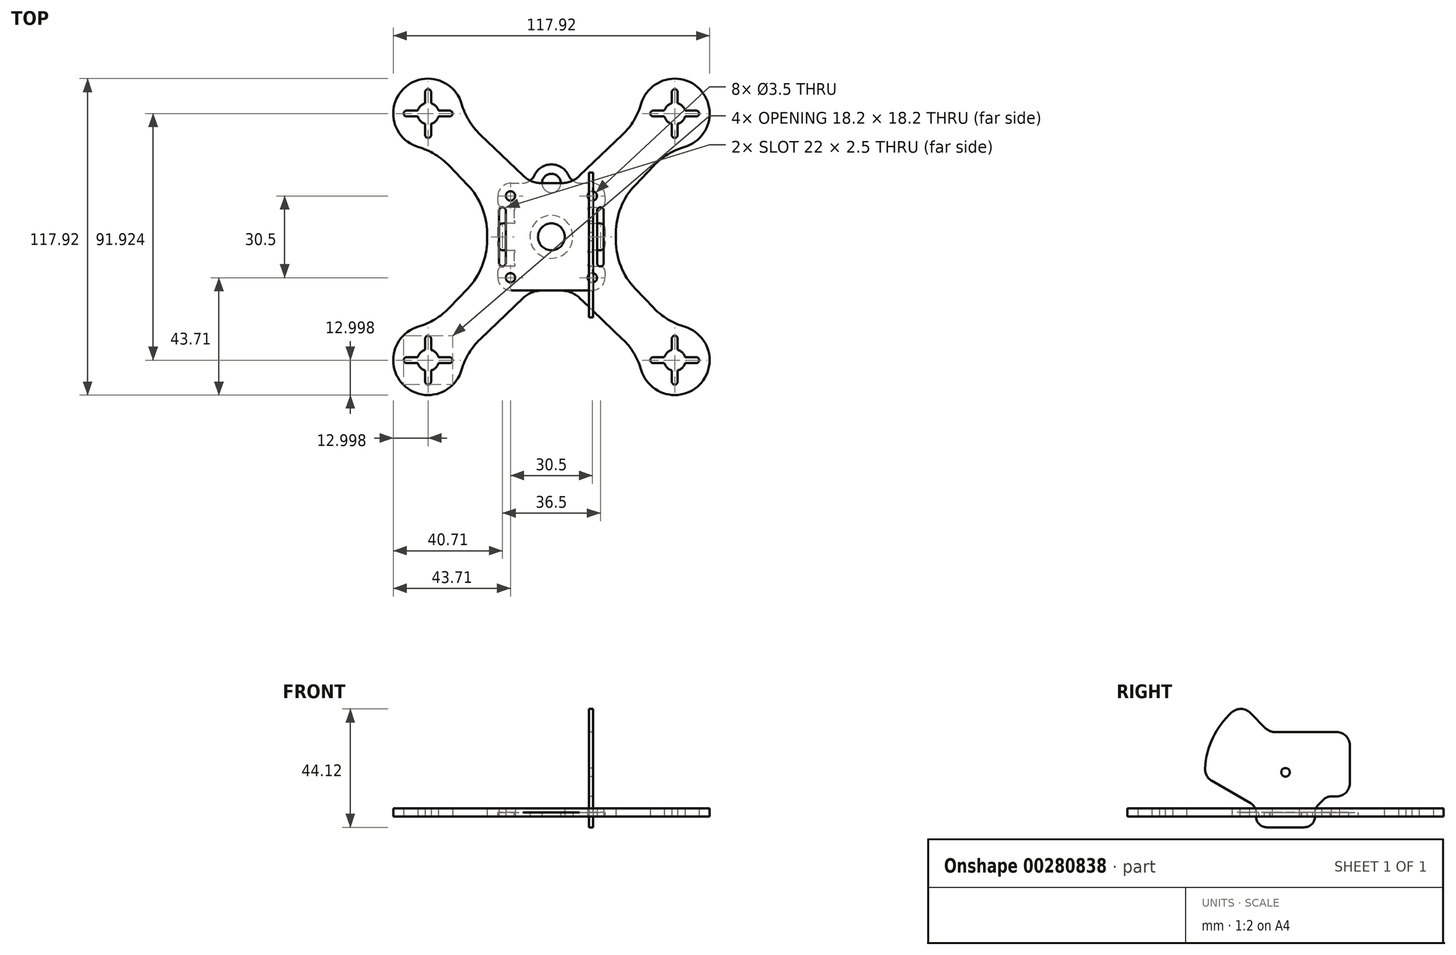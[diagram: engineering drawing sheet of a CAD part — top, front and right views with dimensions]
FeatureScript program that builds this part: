
annotation { "Feature Type Name" : "Feature", "Feature Type Description" : "" }
export const myFeature = defineFeature(function(context is Context, id is Id, definition is map)
    precondition{}
    {
        {
            var Q0;
            Q0=qCreatedBy(makeId("Top.planeOp"),FACE);
            var sketch = newSketch(context, id + "F0", { "sketchPlane" : qUnion([Q0])});
            skCircle(sketch, "E0", {"center": v(-45.96, 45.96) * mm, "radius": 38.1 * mm, "construction": true});
            skCircle(sketch, "E1", {"center": v(45.96, 45.96) * mm, "radius": 38.1 * mm, "construction": true});
            skCircle(sketch, "E2", {"center": v(-45.96, -45.96) * mm, "radius": 38.1 * mm, "construction": true});
            skCircle(sketch, "E3", {"center": v(45.96, -45.96) * mm, "radius": 38.1 * mm, "construction": true});
            skCircle(sketch, "E4", {"center": v(0, 0) * mm, "radius": 65 * mm, "construction": true});
            skLineSegment(sketch, "E5", {"start": v(0, 0) * mm, "end": v(-45.96, 45.96) * mm, "construction": true});
            skLineSegment(sketch, "E6", {"start": v(0, 0) * mm, "end": v(45.96, 45.96) * mm, "construction": true});
            skLineSegment(sketch, "E7", {"start": v(0, 0) * mm, "end": v(45.96, -45.96) * mm, "construction": true});
            skLineSegment(sketch, "E8", {"start": v(0, 0) * mm, "end": v(-45.96, -45.96) * mm, "construction": true});
            skCircle(sketch, "E9", {"center": v(-15.25, 15.25) * mm, "radius": 1.75 * mm});
            skCircle(sketch, "E10", {"center": v(15.25, 15.25) * mm, "radius": 1.75 * mm});
            skCircle(sketch, "E11", {"center": v(15.25, -15.25) * mm, "radius": 1.75 * mm});
            skCircle(sketch, "E12", {"center": v(-15.25, -15.25) * mm, "radius": 1.75 * mm});
            skArc(sketch, "E13", {"start": v(49.6, 33.48) * mm, "mid": v(55.15, 55.15) * mm, "end": v(33.48, 49.6) * mm});
            skLineSegment(sketch, "E14", {"start": v(26.5, 38.1) * mm, "end": v(10.5, 22.78) * mm});
            skLineSegment(sketch, "E15", {"start": v(38.1, 26.5) * mm, "end": v(31.22, 19.32) * mm});
            skPoint(sketch, "E16.visualSharp", {"position": v(33.06, 44.37) * mm});
            skArc(sketch, "E16.filletArc", {"start": v(26.5, 38.1) * mm, "mid": v(30.75, 43.39) * mm, "end": v(33.48, 49.6) * mm});
            skPoint(sketch, "E17.visualSharp", {"position": v(44.37, 33.06) * mm});
            skArc(sketch, "E17.filletArc", {"start": v(49.6, 33.48) * mm, "mid": v(43.39, 30.75) * mm, "end": v(38.1, 26.5) * mm});
            skArc(sketch, "E18", {"start": v(44.86, 49.8) * mm, "mid": v(43.13, 48.8) * mm, "end": v(42.12, 47.06) * mm});
            skLineSegment(sketch, "E19", {"start": v(45.96, 45.96) * mm, "end": v(32.12, 45.96) * mm, "construction": true});
            skLineSegment(sketch, "E20", {"start": v(45.96, 45.96) * mm, "end": v(45.96, 58.96) * mm, "construction": true});
            skLineSegment(sketch, "E21", {"start": v(45.96, 45.96) * mm, "end": v(58.96, 45.96) * mm, "construction": true});
            skLineSegment(sketch, "E22", {"start": v(45.96, 45.96) * mm, "end": v(45.96, 32.12) * mm, "construction": true});
            skArc(sketch, "E23", {"start": v(47.06, 53.96) * mm, "mid": v(45.96, 55.06) * mm, "end": v(44.86, 53.96) * mm});
            skLineSegment(sketch, "E24", {"start": v(44.86, 53.96) * mm, "end": v(44.86, 49.8) * mm});
            skLineSegment(sketch, "E25", {"start": v(47.06, 53.96) * mm, "end": v(47.06, 49.8) * mm});
            skArc(sketch, "E26", {"start": v(53.96, 44.86) * mm, "mid": v(55.06, 45.96) * mm, "end": v(53.96, 47.06) * mm});
            skArc(sketch, "E27", {"start": v(44.86, 37.96) * mm, "mid": v(45.96, 36.86) * mm, "end": v(47.06, 37.96) * mm});
            skArc(sketch, "E28", {"start": v(37.96, 47.06) * mm, "mid": v(36.86, 45.96) * mm, "end": v(37.96, 44.86) * mm});
            skLineSegment(sketch, "E29", {"start": v(44.86, 37.96) * mm, "end": v(44.86, 42.12) * mm});
            skLineSegment(sketch, "E30", {"start": v(37.96, 47.06) * mm, "end": v(42.12, 47.06) * mm});
            skLineSegment(sketch, "E31", {"start": v(37.96, 44.86) * mm, "end": v(42.12, 44.86) * mm});
            skLineSegment(sketch, "E32", {"start": v(53.96, 44.86) * mm, "end": v(49.8, 44.86) * mm});
            skLineSegment(sketch, "E33", {"start": v(47.06, 37.96) * mm, "end": v(47.06, 42.12) * mm});
            skLineSegment(sketch, "E34", {"start": v(53.96, 47.06) * mm, "end": v(49.8, 47.06) * mm});
            skArc(sketch, "E35.trimOffspring", {"start": v(42.12, 44.86) * mm, "mid": v(43.13, 43.13) * mm, "end": v(44.86, 42.12) * mm});
            skArc(sketch, "E36.trimOffspring", {"start": v(47.06, 42.12) * mm, "mid": v(48.8, 43.13) * mm, "end": v(49.8, 44.86) * mm});
            skArc(sketch, "E37.trimOffspring", {"start": v(49.8, 47.06) * mm, "mid": v(48.8, 48.8) * mm, "end": v(47.06, 49.8) * mm});
            skPoint(sketch, "E38.start.orphan", {"position": v(0, 12.73) * mm});
            skPoint(sketch, "E39.orphan", {"position": v(12.73, 0) * mm});
            skPoint(sketch, "E40.1.0", {"position": v(-33.06, 44.37) * mm});
            skPoint(sketch, "E40.1.1", {"position": v(-44.37, 33.06) * mm});
            skArc(sketch, "E40.1.2", {"start": v(-33.48, 49.6) * mm, "mid": v(-55.15, 55.15) * mm, "end": v(-49.6, 33.48) * mm});
            skArc(sketch, "E40.1.3", {"start": v(-33.48, 49.6) * mm, "mid": v(-30.75, 43.39) * mm, "end": v(-26.5, 38.1) * mm});
            skLineSegment(sketch, "E40.1.4", {"start": v(-45.96, 45.96) * mm, "end": v(-45.96, 58.96) * mm, "construction": true});
            skLineSegment(sketch, "E40.1.5", {"start": v(-45.96, 45.96) * mm, "end": v(-32.12, 45.96) * mm, "construction": true});
            skLineSegment(sketch, "E40.1.6", {"start": v(-45.96, 45.96) * mm, "end": v(-45.96, 32.12) * mm, "construction": true});
            skLineSegment(sketch, "E40.1.7", {"start": v(-45.96, 45.96) * mm, "end": v(-58.96, 45.96) * mm, "construction": true});
            skLineSegment(sketch, "E40.1.8", {"start": v(-44.86, 37.96) * mm, "end": v(-44.86, 42.12) * mm});
            skLineSegment(sketch, "E40.1.9", {"start": v(-53.96, 44.86) * mm, "end": v(-49.8, 44.86) * mm});
            skLineSegment(sketch, "E40.1.10", {"start": v(-47.06, 37.96) * mm, "end": v(-47.06, 42.12) * mm});
            skArc(sketch, "E40.1.11", {"start": v(-42.12, 47.06) * mm, "mid": v(-43.13, 48.8) * mm, "end": v(-44.86, 49.8) * mm});
            skLineSegment(sketch, "E40.1.12", {"start": v(-37.96, 47.06) * mm, "end": v(-42.12, 47.06) * mm});
            skArc(sketch, "E40.1.13", {"start": v(-47.06, 37.96) * mm, "mid": v(-45.96, 36.86) * mm, "end": v(-44.86, 37.96) * mm});
            skArc(sketch, "E40.1.14", {"start": v(-37.96, 44.86) * mm, "mid": v(-36.86, 45.96) * mm, "end": v(-37.96, 47.06) * mm});
            skLineSegment(sketch, "E40.1.15", {"start": v(-44.86, 53.96) * mm, "end": v(-44.86, 49.8) * mm});
            skLineSegment(sketch, "E40.1.16", {"start": v(-47.06, 53.96) * mm, "end": v(-47.06, 49.8) * mm});
            skArc(sketch, "E40.1.17", {"start": v(-47.06, 49.8) * mm, "mid": v(-48.8, 48.8) * mm, "end": v(-49.8, 47.06) * mm});
            skLineSegment(sketch, "E40.1.18", {"start": v(-53.96, 47.06) * mm, "end": v(-49.8, 47.06) * mm});
            skArc(sketch, "E40.1.19", {"start": v(-53.96, 47.06) * mm, "mid": v(-55.06, 45.96) * mm, "end": v(-53.96, 44.86) * mm});
            skArc(sketch, "E40.1.20", {"start": v(-44.86, 42.12) * mm, "mid": v(-43.13, 43.13) * mm, "end": v(-42.12, 44.86) * mm});
            skLineSegment(sketch, "E40.1.21", {"start": v(-37.96, 44.86) * mm, "end": v(-42.12, 44.86) * mm});
            skArc(sketch, "E40.1.22", {"start": v(-49.8, 44.86) * mm, "mid": v(-48.8, 43.13) * mm, "end": v(-47.06, 42.12) * mm});
            skArc(sketch, "E40.1.23", {"start": v(-44.86, 53.96) * mm, "mid": v(-45.96, 55.06) * mm, "end": v(-47.06, 53.96) * mm});
            skArc(sketch, "E40.1.24", {"start": v(-38.1, 26.5) * mm, "mid": v(-43.39, 30.75) * mm, "end": v(-49.6, 33.48) * mm});
            skLineSegment(sketch, "E40.1.25", {"start": v(-38.1, 26.5) * mm, "end": v(-31.22, 19.32) * mm});
            skLineSegment(sketch, "E40.1.26", {"start": v(-26.5, 38.1) * mm, "end": v(-10.5, 22.78) * mm});
            skPoint(sketch, "E40.2.0", {"position": v(-44.37, -33.06) * mm});
            skPoint(sketch, "E40.2.1", {"position": v(-33.06, -44.37) * mm});
            skArc(sketch, "E40.2.2", {"start": v(-49.6, -33.48) * mm, "mid": v(-55.15, -55.15) * mm, "end": v(-33.48, -49.6) * mm});
            skArc(sketch, "E40.2.3", {"start": v(-49.6, -33.48) * mm, "mid": v(-43.39, -30.75) * mm, "end": v(-38.1, -26.5) * mm});
            skLineSegment(sketch, "E40.2.4", {"start": v(-45.96, -45.96) * mm, "end": v(-58.96, -45.96) * mm, "construction": true});
            skLineSegment(sketch, "E40.2.5", {"start": v(-45.96, -45.96) * mm, "end": v(-45.96, -32.12) * mm, "construction": true});
            skLineSegment(sketch, "E40.2.6", {"start": v(-45.96, -45.96) * mm, "end": v(-32.12, -45.96) * mm, "construction": true});
            skLineSegment(sketch, "E40.2.7", {"start": v(-45.96, -45.96) * mm, "end": v(-45.96, -58.96) * mm, "construction": true});
            skLineSegment(sketch, "E40.2.8", {"start": v(-37.96, -44.86) * mm, "end": v(-42.12, -44.86) * mm});
            skLineSegment(sketch, "E40.2.9", {"start": v(-44.86, -53.96) * mm, "end": v(-44.86, -49.8) * mm});
            skLineSegment(sketch, "E40.2.10", {"start": v(-37.96, -47.06) * mm, "end": v(-42.12, -47.06) * mm});
            skArc(sketch, "E40.2.11", {"start": v(-47.06, -42.12) * mm, "mid": v(-48.8, -43.13) * mm, "end": v(-49.8, -44.86) * mm});
            skLineSegment(sketch, "E40.2.12", {"start": v(-47.06, -37.96) * mm, "end": v(-47.06, -42.12) * mm});
            skArc(sketch, "E40.2.13", {"start": v(-37.96, -47.06) * mm, "mid": v(-36.86, -45.96) * mm, "end": v(-37.96, -44.86) * mm});
            skArc(sketch, "E40.2.14", {"start": v(-44.86, -37.96) * mm, "mid": v(-45.96, -36.86) * mm, "end": v(-47.06, -37.96) * mm});
            skLineSegment(sketch, "E40.2.15", {"start": v(-53.96, -44.86) * mm, "end": v(-49.8, -44.86) * mm});
            skLineSegment(sketch, "E40.2.16", {"start": v(-53.96, -47.06) * mm, "end": v(-49.8, -47.06) * mm});
            skArc(sketch, "E40.2.17", {"start": v(-49.8, -47.06) * mm, "mid": v(-48.8, -48.8) * mm, "end": v(-47.06, -49.8) * mm});
            skLineSegment(sketch, "E40.2.18", {"start": v(-47.06, -53.96) * mm, "end": v(-47.06, -49.8) * mm});
            skArc(sketch, "E40.2.19", {"start": v(-47.06, -53.96) * mm, "mid": v(-45.96, -55.06) * mm, "end": v(-44.86, -53.96) * mm});
            skArc(sketch, "E40.2.20", {"start": v(-42.12, -44.86) * mm, "mid": v(-43.13, -43.13) * mm, "end": v(-44.86, -42.12) * mm});
            skLineSegment(sketch, "E40.2.21", {"start": v(-44.86, -37.96) * mm, "end": v(-44.86, -42.12) * mm});
            skArc(sketch, "E40.2.22", {"start": v(-44.86, -49.8) * mm, "mid": v(-43.13, -48.8) * mm, "end": v(-42.12, -47.06) * mm});
            skArc(sketch, "E40.2.23", {"start": v(-53.96, -44.86) * mm, "mid": v(-55.06, -45.96) * mm, "end": v(-53.96, -47.06) * mm});
            skArc(sketch, "E40.2.24", {"start": v(-26.5, -38.1) * mm, "mid": v(-30.75, -43.39) * mm, "end": v(-33.48, -49.6) * mm});
            skLineSegment(sketch, "E40.2.25", {"start": v(-26.5, -38.1) * mm, "end": v(-10.5, -22.78) * mm});
            skLineSegment(sketch, "E40.2.26", {"start": v(-38.1, -26.5) * mm, "end": v(-31.22, -19.32) * mm});
            skPoint(sketch, "E40.3.0", {"position": v(33.06, -44.37) * mm});
            skPoint(sketch, "E40.3.1", {"position": v(44.37, -33.06) * mm});
            skArc(sketch, "E40.3.2", {"start": v(33.48, -49.6) * mm, "mid": v(55.15, -55.15) * mm, "end": v(49.6, -33.48) * mm});
            skArc(sketch, "E40.3.3", {"start": v(33.48, -49.6) * mm, "mid": v(30.75, -43.39) * mm, "end": v(26.5, -38.1) * mm});
            skLineSegment(sketch, "E40.3.4", {"start": v(45.96, -45.96) * mm, "end": v(45.96, -58.96) * mm, "construction": true});
            skLineSegment(sketch, "E40.3.5", {"start": v(45.96, -45.96) * mm, "end": v(32.12, -45.96) * mm, "construction": true});
            skLineSegment(sketch, "E40.3.6", {"start": v(45.96, -45.96) * mm, "end": v(45.96, -32.12) * mm, "construction": true});
            skLineSegment(sketch, "E40.3.7", {"start": v(45.96, -45.96) * mm, "end": v(58.96, -45.96) * mm, "construction": true});
            skLineSegment(sketch, "E40.3.8", {"start": v(44.86, -37.96) * mm, "end": v(44.86, -42.12) * mm});
            skLineSegment(sketch, "E40.3.9", {"start": v(53.96, -44.86) * mm, "end": v(49.8, -44.86) * mm});
            skLineSegment(sketch, "E40.3.10", {"start": v(47.06, -37.96) * mm, "end": v(47.06, -42.12) * mm});
            skArc(sketch, "E40.3.11", {"start": v(42.12, -47.06) * mm, "mid": v(43.13, -48.8) * mm, "end": v(44.86, -49.8) * mm});
            skLineSegment(sketch, "E40.3.12", {"start": v(37.96, -47.06) * mm, "end": v(42.12, -47.06) * mm});
            skArc(sketch, "E40.3.13", {"start": v(47.06, -37.96) * mm, "mid": v(45.96, -36.86) * mm, "end": v(44.86, -37.96) * mm});
            skArc(sketch, "E40.3.14", {"start": v(37.96, -44.86) * mm, "mid": v(36.86, -45.96) * mm, "end": v(37.96, -47.06) * mm});
            skLineSegment(sketch, "E40.3.15", {"start": v(44.86, -53.96) * mm, "end": v(44.86, -49.8) * mm});
            skLineSegment(sketch, "E40.3.16", {"start": v(47.06, -53.96) * mm, "end": v(47.06, -49.8) * mm});
            skArc(sketch, "E40.3.17", {"start": v(47.06, -49.8) * mm, "mid": v(48.8, -48.8) * mm, "end": v(49.8, -47.06) * mm});
            skLineSegment(sketch, "E40.3.18", {"start": v(53.96, -47.06) * mm, "end": v(49.8, -47.06) * mm});
            skArc(sketch, "E40.3.19", {"start": v(53.96, -47.06) * mm, "mid": v(55.06, -45.96) * mm, "end": v(53.96, -44.86) * mm});
            skArc(sketch, "E40.3.20", {"start": v(44.86, -42.12) * mm, "mid": v(43.13, -43.13) * mm, "end": v(42.12, -44.86) * mm});
            skLineSegment(sketch, "E40.3.21", {"start": v(37.96, -44.86) * mm, "end": v(42.12, -44.86) * mm});
            skArc(sketch, "E40.3.22", {"start": v(49.8, -44.86) * mm, "mid": v(48.8, -43.13) * mm, "end": v(47.06, -42.12) * mm});
            skArc(sketch, "E40.3.23", {"start": v(44.86, -53.96) * mm, "mid": v(45.96, -55.06) * mm, "end": v(47.06, -53.96) * mm});
            skArc(sketch, "E40.3.24", {"start": v(38.1, -26.5) * mm, "mid": v(43.39, -30.75) * mm, "end": v(49.6, -33.48) * mm});
            skLineSegment(sketch, "E40.3.25", {"start": v(38.1, -26.5) * mm, "end": v(31.22, -19.32) * mm});
            skLineSegment(sketch, "E40.3.26", {"start": v(26.5, -38.1) * mm, "end": v(10.5, -22.78) * mm});
            skLineSegment(sketch, "E41.trimOffspring", {"start": v(-3.58, 20) * mm, "end": v(3.58, 20) * mm});
            skLineSegment(sketch, "E42.trimOffspring", {"start": v(-3.58, -20) * mm, "end": v(3.58, -20) * mm});
            skLineSegment(sketch, "E43.bottom", {"start": v(-19.5, 11) * mm, "end": v(-17, 11) * mm});
            skLineSegment(sketch, "E43.top", {"start": v(-19.5, -11) * mm, "end": v(-17, -11) * mm});
            skLineSegment(sketch, "E43.right", {"start": v(-17, 11) * mm, "end": v(-17, -11) * mm});
            skLineSegment(sketch, "E44.bottom", {"start": v(19.5, 11) * mm, "end": v(17, 11) * mm});
            skLineSegment(sketch, "E44.top", {"start": v(19.5, -11) * mm, "end": v(17, -11) * mm});
            skLineSegment(sketch, "E44.right", {"start": v(17, 11) * mm, "end": v(17, -11) * mm});
            skLineSegment(sketch, "E45", {"start": v(-19.5, 11) * mm, "end": v(-19.5, -11) * mm});
            skLineSegment(sketch, "E46", {"start": v(19.5, 11) * mm, "end": v(19.5, -11) * mm});
            skLineSegment(sketch, "E47", {"start": v(-24, 1.34) * mm, "end": v(-24, -1.34) * mm});
            skLineSegment(sketch, "E48", {"start": v(24, 1.34) * mm, "end": v(24, -1.34) * mm});
            skPoint(sketch, "E49.visualSharp", {"position": v(-24, 11.78) * mm});
            skArc(sketch, "E49.filletArc", {"start": v(-24, 1.34) * mm, "mid": v(-25.87, 11.02) * mm, "end": v(-31.22, 19.32) * mm});
            skPoint(sketch, "E50.visualSharp", {"position": v(-24, -11.78) * mm});
            skArc(sketch, "E50.filletArc", {"start": v(-31.22, -19.32) * mm, "mid": v(-25.87, -11.02) * mm, "end": v(-24, -1.34) * mm});
            skPoint(sketch, "E51.visualSharp", {"position": v(24, -11.78) * mm});
            skArc(sketch, "E51.filletArc", {"start": v(24, -1.34) * mm, "mid": v(25.87, -11.02) * mm, "end": v(31.22, -19.32) * mm});
            skPoint(sketch, "E52.visualSharp", {"position": v(24, 11.78) * mm});
            skArc(sketch, "E52.filletArc", {"start": v(31.22, 19.32) * mm, "mid": v(25.87, 11.02) * mm, "end": v(24, 1.34) * mm});
            skPoint(sketch, "E53.visualSharp", {"position": v(-7.6, 20) * mm});
            skArc(sketch, "E53.filletArc", {"start": v(-10.5, 22.78) * mm, "mid": v(-7.3, 20.72) * mm, "end": v(-3.58, 20) * mm});
            skPoint(sketch, "E54.visualSharp", {"position": v(7.6, 20) * mm});
            skArc(sketch, "E54.filletArc", {"start": v(3.58, 20) * mm, "mid": v(7.3, 20.72) * mm, "end": v(10.5, 22.78) * mm});
            skPoint(sketch, "E55.visualSharp", {"position": v(-7.6, -20) * mm});
            skArc(sketch, "E55.filletArc", {"start": v(-3.58, -20) * mm, "mid": v(-7.3, -20.72) * mm, "end": v(-10.5, -22.78) * mm});
            skPoint(sketch, "E56.visualSharp", {"position": v(7.6, -20) * mm});
            skArc(sketch, "E56.filletArc", {"start": v(10.5, -22.78) * mm, "mid": v(7.3, -20.72) * mm, "end": v(3.58, -20) * mm});
            skCircle(sketch, "E57", {"center": v(0, 0) * mm, "radius": 5 * mm});
            skSolve(sketch);
        }
        {
            var Q0;
            Q0 = qSketchRegion(id + "F0", true);
            extrude(context, id + "F1", {"entities" : qUnion([Q0]), "depth" : 3 * mm});
        }
        {
            var Q0;
            Q0=qCreatedBy(makeId("Top.planeOp"),FACE);
            var sketch = newSketch(context, id + "F2", { "sketchPlane" : qUnion([Q0])});
            skLineSegment(sketch, "E58.bottom", {"start": v(-15, 20) * mm, "end": v(-10.9, 20) * mm});
            skLineSegment(sketch, "E58.top", {"start": v(-15, -20) * mm, "end": v(15, -20) * mm});
            skLineSegment(sketch, "E58.left", {"start": v(-20, 15) * mm, "end": v(-20, 13) * mm});
            skLineSegment(sketch, "E58.right", {"start": v(20, 15) * mm, "end": v(20, 13) * mm});
            skLineSegment(sketch, "E59", {"start": v(-20, 20) * mm, "end": v(20, -20) * mm, "construction": true});
            skLineSegment(sketch, "E60", {"start": v(-20, -20) * mm, "end": v(20, 20) * mm, "construction": true});
            skPoint(sketch, "E61.visualSharp", {"position": v(-20, 20) * mm});
            skArc(sketch, "E61.filletArc", {"start": v(-15, 20) * mm, "mid": v(-18.54, 18.54) * mm, "end": v(-20, 15) * mm});
            skPoint(sketch, "E62.visualSharp", {"position": v(20, 20) * mm});
            skArc(sketch, "E62.filletArc", {"start": v(20, 15) * mm, "mid": v(18.54, 18.54) * mm, "end": v(15, 20) * mm});
            skPoint(sketch, "E63.visualSharp", {"position": v(20, -20) * mm});
            skArc(sketch, "E63.filletArc", {"start": v(15, -20) * mm, "mid": v(18.54, -18.54) * mm, "end": v(20, -15) * mm});
            skPoint(sketch, "E64.visualSharp", {"position": v(-20, -20) * mm});
            skArc(sketch, "E64.filletArc", {"start": v(-20, -15) * mm, "mid": v(-18.54, -18.54) * mm, "end": v(-15, -20) * mm});
            skCircle(sketch, "E65", {"center": v(-15.25, -15.25) * mm, "radius": 1.75 * mm});
            skCircle(sketch, "E66", {"center": v(15.25, -15.25) * mm, "radius": 1.75 * mm});
            skCircle(sketch, "E67", {"center": v(15.25, 15.25) * mm, "radius": 1.75 * mm});
            skCircle(sketch, "E68", {"center": v(-15.25, 15.25) * mm, "radius": 1.75 * mm});
            skLineSegment(sketch, "E69", {"start": v(14, 10) * mm, "end": v(14, 6) * mm});
            skLineSegment(sketch, "E70", {"start": v(-14, 10) * mm, "end": v(-14, 6) * mm});
            skLineSegment(sketch, "E71", {"start": v(14, 11) * mm, "end": v(18, 11) * mm});
            skLineSegment(sketch, "E72", {"start": v(14, -11) * mm, "end": v(18, -11) * mm});
            skLineSegment(sketch, "E73", {"start": v(-14, 11) * mm, "end": v(-18, 11) * mm});
            skLineSegment(sketch, "E74", {"start": v(-14, -11) * mm, "end": v(-18, -11) * mm});
            skLineSegment(sketch, "E75.trimOffspring", {"start": v(-20, -13) * mm, "end": v(-20, -15) * mm});
            skLineSegment(sketch, "E76.trimOffspring", {"start": v(20, -13) * mm, "end": v(20, -15) * mm});
            skLineSegment(sketch, "E77", {"start": v(-14, 5) * mm, "end": v(-18, 5) * mm});
            skLineSegment(sketch, "E78", {"start": v(-20, 3) * mm, "end": v(-20, -3) * mm});
            skLineSegment(sketch, "E79", {"start": v(-18, -5) * mm, "end": v(-14, -5) * mm});
            skLineSegment(sketch, "E80", {"start": v(14, 5) * mm, "end": v(18, 5) * mm});
            skLineSegment(sketch, "E81", {"start": v(20, 3) * mm, "end": v(20, -3) * mm});
            skLineSegment(sketch, "E82", {"start": v(18, -5) * mm, "end": v(14, -5) * mm});
            skLineSegment(sketch, "E83.trimOffspring", {"start": v(-14, -6) * mm, "end": v(-14, -10) * mm});
            skLineSegment(sketch, "E84.trimOffspring", {"start": v(14, -6) * mm, "end": v(14, -10) * mm});
            skArc(sketch, "E85", {"start": v(-14, 5) * mm, "mid": v(-13.5, 5.5) * mm, "end": v(-14, 6) * mm});
            skArc(sketch, "E86", {"start": v(-14, 10) * mm, "mid": v(-13.5, 10.5) * mm, "end": v(-14, 11) * mm});
            skArc(sketch, "E87", {"start": v(-14, -6) * mm, "mid": v(-13.5, -5.5) * mm, "end": v(-14, -5) * mm});
            skArc(sketch, "E88", {"start": v(-14, -11) * mm, "mid": v(-13.5, -10.5) * mm, "end": v(-14, -10) * mm});
            skArc(sketch, "E89", {"start": v(14, -5) * mm, "mid": v(13.5, -5.5) * mm, "end": v(14, -6) * mm});
            skArc(sketch, "E90", {"start": v(14, -10) * mm, "mid": v(13.5, -10.5) * mm, "end": v(14, -11) * mm});
            skArc(sketch, "E91", {"start": v(14, 11) * mm, "mid": v(13.5, 10.5) * mm, "end": v(14, 10) * mm});
            skArc(sketch, "E92", {"start": v(14, 6) * mm, "mid": v(13.5, 5.5) * mm, "end": v(14, 5) * mm});
            skPoint(sketch, "E93.visualSharp", {"position": v(-20, 5) * mm});
            skArc(sketch, "E93.filletArc", {"start": v(-18, 5) * mm, "mid": v(-19.41, 4.41) * mm, "end": v(-20, 3) * mm});
            skPoint(sketch, "E94.visualSharp", {"position": v(-20, -5) * mm});
            skArc(sketch, "E94.filletArc", {"start": v(-20, -3) * mm, "mid": v(-19.41, -4.41) * mm, "end": v(-18, -5) * mm});
            skPoint(sketch, "E95.visualSharp", {"position": v(-20, -11) * mm});
            skArc(sketch, "E95.filletArc", {"start": v(-18, -11) * mm, "mid": v(-19.41, -11.59) * mm, "end": v(-20, -13) * mm});
            skPoint(sketch, "E96.visualSharp", {"position": v(-20, 11) * mm});
            skArc(sketch, "E96.filletArc", {"start": v(-20, 13) * mm, "mid": v(-19.41, 11.59) * mm, "end": v(-18, 11) * mm});
            skPoint(sketch, "E97.visualSharp", {"position": v(20, 11) * mm});
            skArc(sketch, "E97.filletArc", {"start": v(18, 11) * mm, "mid": v(19.41, 11.59) * mm, "end": v(20, 13) * mm});
            skPoint(sketch, "E98.visualSharp", {"position": v(20, 5) * mm});
            skArc(sketch, "E98.filletArc", {"start": v(20, 3) * mm, "mid": v(19.41, 4.41) * mm, "end": v(18, 5) * mm});
            skPoint(sketch, "E99.visualSharp", {"position": v(20, -5) * mm});
            skArc(sketch, "E99.filletArc", {"start": v(18, -5) * mm, "mid": v(19.41, -4.41) * mm, "end": v(20, -3) * mm});
            skPoint(sketch, "E100.visualSharp", {"position": v(20, -11) * mm});
            skArc(sketch, "E100.filletArc", {"start": v(20, -13) * mm, "mid": v(19.41, -11.59) * mm, "end": v(18, -11) * mm});
            skCircle(sketch, "E101", {"center": v(0, 0) * mm, "radius": 8 * mm});
            skCircle(sketch, "E102", {"center": v(0, 20) * mm, "radius": 3.5 * mm});
            skArc(sketch, "E103", {"start": v(6.36, 22.92) * mm, "mid": v(0, 27) * mm, "end": v(-6.36, 22.92) * mm});
            skLineSegment(sketch, "E104.trimOffspring", {"start": v(10.9, 20) * mm, "end": v(15, 20) * mm});
            skPoint(sketch, "E105.visualSharp", {"position": v(-7, 20) * mm});
            skArc(sketch, "E105.filletArc", {"start": v(-10.9, 20) * mm, "mid": v(-8.2, 20.8) * mm, "end": v(-6.36, 22.92) * mm});
            skPoint(sketch, "E106.visualSharp", {"position": v(7, 20) * mm});
            skArc(sketch, "E106.filletArc", {"start": v(6.36, 22.92) * mm, "mid": v(8.2, 20.8) * mm, "end": v(10.9, 20) * mm});
            skSolve(sketch);
        }
        {
            var Q0;
            Q0 = qSketchRegion(id + "F2", true);
            extrude(context, id + "F3", {"entities" : qUnion([Q0]), "depth" : 1.5 * mm});
        }
        {
            var Q0;
            Q0=makeQuery(id+"F1.opExtrude","SWEPT_EDGE",EDGE,{"disambiguationData":[OSD([sQuery(id+"F0.wireOp",EDGE,"E43.bottom"),sQuery(id+"F0.wireOp",EDGE,"E45")])]});
            var Q1;
            Q1=makeQuery(id+"F1.opExtrude","SWEPT_EDGE",EDGE,{"disambiguationData":[OSD([sQuery(id+"F0.wireOp",EDGE,"E43.bottom"),sQuery(id+"F0.wireOp",EDGE,"E43.right")])]});
            var Q2;
            Q2=makeQuery(id+"F1.opExtrude","SWEPT_EDGE",EDGE,{"disambiguationData":[OSD([sQuery(id+"F0.wireOp",EDGE,"E43.top"),sQuery(id+"F0.wireOp",EDGE,"E45")])]});
            var Q3;
            Q3=makeQuery(id+"F1.opExtrude","SWEPT_EDGE",EDGE,{"disambiguationData":[OSD([sQuery(id+"F0.wireOp",EDGE,"E43.top"),sQuery(id+"F0.wireOp",EDGE,"E43.right")])]});
            var Q4;
            Q4=makeQuery(id+"F1.opExtrude","SWEPT_EDGE",EDGE,{"disambiguationData":[OSD([sQuery(id+"F0.wireOp",EDGE,"E44.top"),sQuery(id+"F0.wireOp",EDGE,"E44.right")])]});
            var Q5;
            Q5=makeQuery(id+"F1.opExtrude","SWEPT_EDGE",EDGE,{"disambiguationData":[OSD([sQuery(id+"F0.wireOp",EDGE,"E44.top"),sQuery(id+"F0.wireOp",EDGE,"E46")])]});
            var Q6;
            Q6=makeQuery(id+"F1.opExtrude","SWEPT_EDGE",EDGE,{"disambiguationData":[OSD([sQuery(id+"F0.wireOp",EDGE,"E44.bottom"),sQuery(id+"F0.wireOp",EDGE,"E44.right")])]});
            var Q7;
            Q7=makeQuery(id+"F1.opExtrude","SWEPT_EDGE",EDGE,{"disambiguationData":[OSD([sQuery(id+"F0.wireOp",EDGE,"E44.bottom"),sQuery(id+"F0.wireOp",EDGE,"E46")])]});
            fillet(context, id + "F4", {"entities" : qUnion([Q0, Q1, Q2, Q3, Q4, Q5, Q6, Q7]), "radius" : 1.25 * mm, "tangentPropagation" : true, "allowEdgeOverflow" : false});
        }
        {
            var Q0;
            Q0=qCreatedBy(makeId("Right.planeOp"),FACE);
            cPlane(context, id + "F5", {"entities" : qUnion([Q0]), "cplaneType" : CPlaneType.OFFSET, "offset" : 14 * mm, "width" : 150 * mm, "height" : 150 * mm});
        }
        {
            var Q0;
            Q0=qCreatedBy(id+"F5.planeOp",FACE);
            var sketch = newSketch(context, id + "F6", { "sketchPlane" : qUnion([Q0])});
            skLineSegment(sketch, "E107.bottom", {"start": v(-5.75, 1.5) * mm, "end": v(5.75, 1.5) * mm});
            skLineSegment(sketch, "E107.top", {"start": v(-5.75, 0) * mm, "end": v(5.75, 0) * mm});
            skLineSegment(sketch, "E107.left", {"start": v(-5.75, 1.5) * mm, "end": v(-5.75, 0) * mm});
            skLineSegment(sketch, "E107.right", {"start": v(5.75, 1.5) * mm, "end": v(5.75, 0) * mm});
            skLineSegment(sketch, "E108.top", {"start": v(-7, -4) * mm, "end": v(7, -4) * mm});
            skLineSegment(sketch, "E108.left", {"start": v(-11, 1.5) * mm, "end": v(-11, 0) * mm});
            skLineSegment(sketch, "E108.right", {"start": v(11, 1.5) * mm, "end": v(11, 0) * mm});
            skArc(sketch, "E109", {"start": v(-11, 1.5) * mm, "mid": v(-11.54, 3.5) * mm, "end": v(-13, 4.96) * mm});
            skArc(sketch, "E110", {"start": v(12.17, 4.33) * mm, "mid": v(11.3, 3.03) * mm, "end": v(11, 1.5) * mm});
            skCircle(sketch, "E111", {"center": v(0, 16.5) * mm, "radius": 1.6 * mm});
            skLineSegment(sketch, "E112", {"start": v(0, 16.5) * mm, "end": v(-25.98, 31.5) * mm, "construction": true});
            skArc(sketch, "E113", {"start": v(-20.02, 38.84) * mm, "mid": v(-27.1, 29.36) * mm, "end": v(-29.97, 17.88) * mm});
            skLineSegment(sketch, "E114", {"start": v(0, 16.5) * mm, "end": v(-22.98, 35.78) * mm, "construction": true});
            skLineSegment(sketch, "E115", {"start": v(0, 16.5) * mm, "end": v(-28.2, 26.76) * mm, "construction": true});
            skLineSegment(sketch, "E116", {"start": v(0, 16.5) * mm, "end": v(-21.21, 37.71) * mm, "construction": true});
            skLineSegment(sketch, "E117", {"start": v(-13, 4.96) * mm, "end": v(-27.47, 13.32) * mm});
            skLineSegment(sketch, "E118", {"start": v(-7.46, 32.96) * mm, "end": v(-13.15, 38.65) * mm});
            skLineSegment(sketch, "E119.trimOffspring", {"start": v(-3.93, 31.5) * mm, "end": v(19, 31.5) * mm});
            skLineSegment(sketch, "E120", {"start": v(24, 26.5) * mm, "end": v(24, 12.5) * mm});
            skLineSegment(sketch, "E121", {"start": v(19, 7.5) * mm, "end": v(17, 7.5) * mm});
            skLineSegment(sketch, "E122", {"start": v(14.17, 6.33) * mm, "end": v(12.17, 4.33) * mm});
            skPoint(sketch, "E123.visualSharp", {"position": v(-11, -4) * mm});
            skArc(sketch, "E123.filletArc", {"start": v(-11, 0) * mm, "mid": v(-9.83, -2.83) * mm, "end": v(-7, -4) * mm});
            skPoint(sketch, "E124.visualSharp", {"position": v(11, -4) * mm});
            skArc(sketch, "E124.filletArc", {"start": v(7, -4) * mm, "mid": v(9.83, -2.83) * mm, "end": v(11, 0) * mm});
            skPoint(sketch, "E125.visualSharp", {"position": v(-29.95, 14.75) * mm});
            skArc(sketch, "E125.filletArc", {"start": v(-29.97, 17.88) * mm, "mid": v(-29.36, 15.25) * mm, "end": v(-27.47, 13.32) * mm});
            skPoint(sketch, "E126.visualSharp", {"position": v(-16.23, 41.73) * mm});
            skArc(sketch, "E126.filletArc", {"start": v(-13.15, 38.65) * mm, "mid": v(-16.55, 40.11) * mm, "end": v(-20.02, 38.84) * mm});
            skPoint(sketch, "E127.visualSharp", {"position": v(-6, 31.5) * mm});
            skArc(sketch, "E127.filletArc", {"start": v(-7.46, 32.96) * mm, "mid": v(-5.84, 31.88) * mm, "end": v(-3.93, 31.5) * mm});
            skPoint(sketch, "E128.visualSharp", {"position": v(24, 31.5) * mm});
            skArc(sketch, "E128.filletArc", {"start": v(24, 26.5) * mm, "mid": v(22.54, 30.04) * mm, "end": v(19, 31.5) * mm});
            skPoint(sketch, "E129.visualSharp", {"position": v(24, 7.5) * mm});
            skArc(sketch, "E129.filletArc", {"start": v(19, 7.5) * mm, "mid": v(22.54, 8.96) * mm, "end": v(24, 12.5) * mm});
            skPoint(sketch, "E130.visualSharp", {"position": v(15.34, 7.5) * mm});
            skArc(sketch, "E130.filletArc", {"start": v(17, 7.5) * mm, "mid": v(15.47, 7.2) * mm, "end": v(14.17, 6.33) * mm});
            skSolve(sketch);
        }
        {
            var Q0;
            Q0 = qSketchRegion(id + "F6", true);
            extrude(context, id + "F7", {"entities" : qUnion([Q0]), "depth" : 1.5 * mm});
        }
    });
